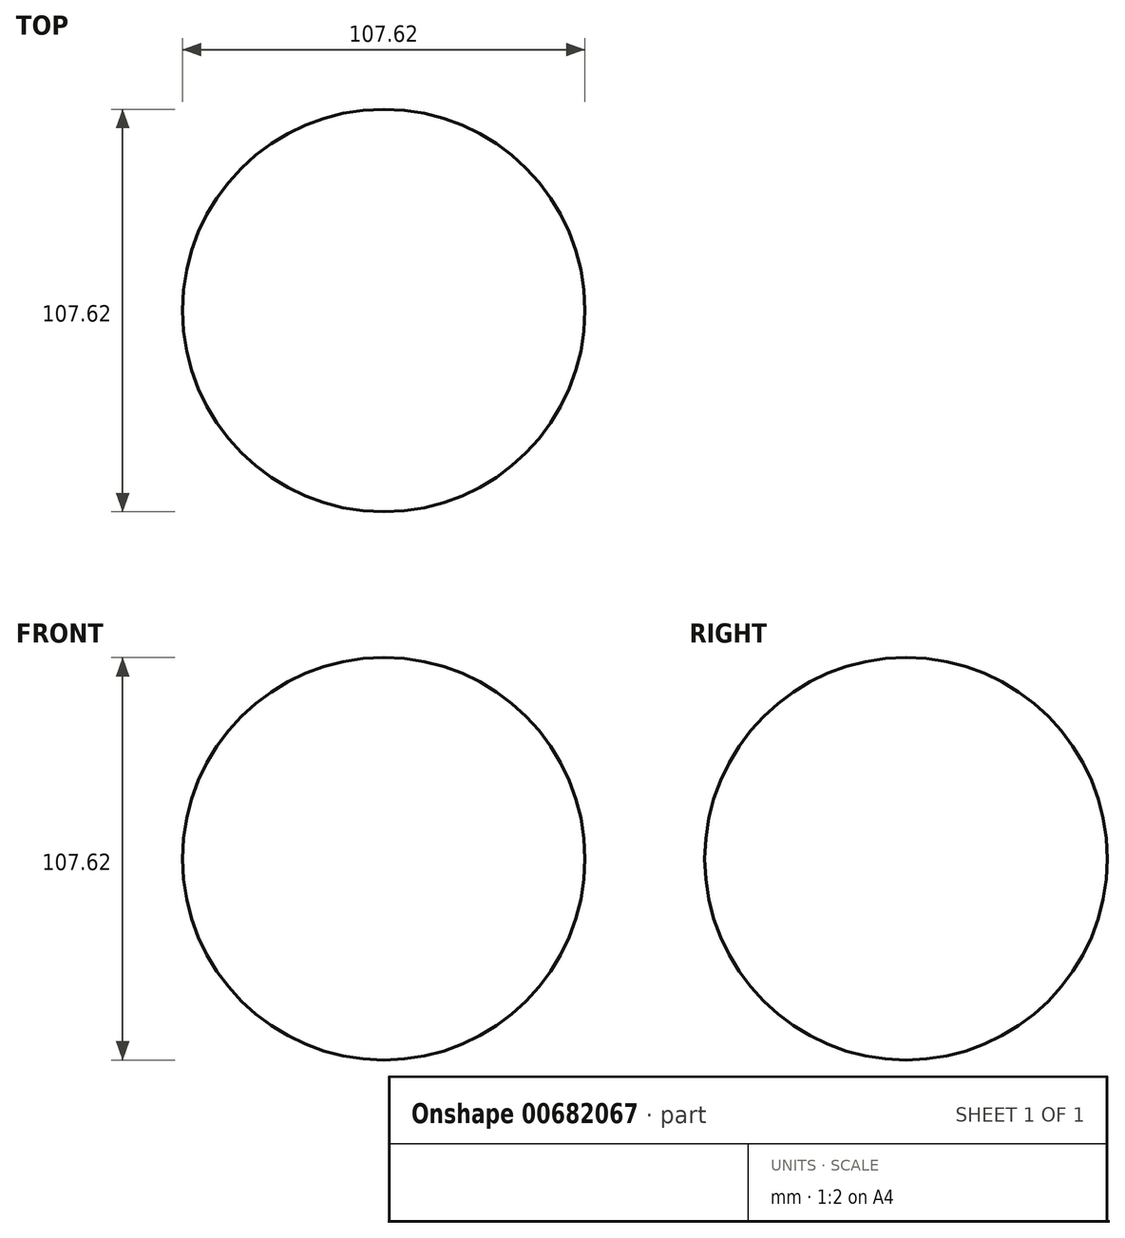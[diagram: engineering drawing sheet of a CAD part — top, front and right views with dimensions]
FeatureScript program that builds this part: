
annotation { "Feature Type Name" : "Feature", "Feature Type Description" : "" }
export const myFeature = defineFeature(function(context is Context, id is Id, definition is map)
    precondition{}
    {
        {
            var Q0;
            Q0=qCreatedBy(makeId("Front.planeOp"),FACE);
            var sketch = newSketch(context, id + "F0", { "sketchPlane" : qUnion([Q0])});
            skArc(sketch, "E0", {"start": v(0, 53.8) * mm, "mid": v(-53.8, 0) * mm, "end": v(0, -53.8) * mm});
            skLineSegment(sketch, "E1", {"start": v(0, 53.8) * mm, "end": v(0, -53.8) * mm});
            skSolve(sketch);
        }
        {
            var Q0;
            Q0 = qSketchRegion(id + "F0", true);
            var Q1;
            Q1=sQuery(id+"F0.wireOp",EDGE,"E1");
            revolve(context, id + "F1", {"entities" : qUnion([Q0]), "axis" : qUnion([Q1]), "revolveType" : RevolveType.FULL});
        }
    });
